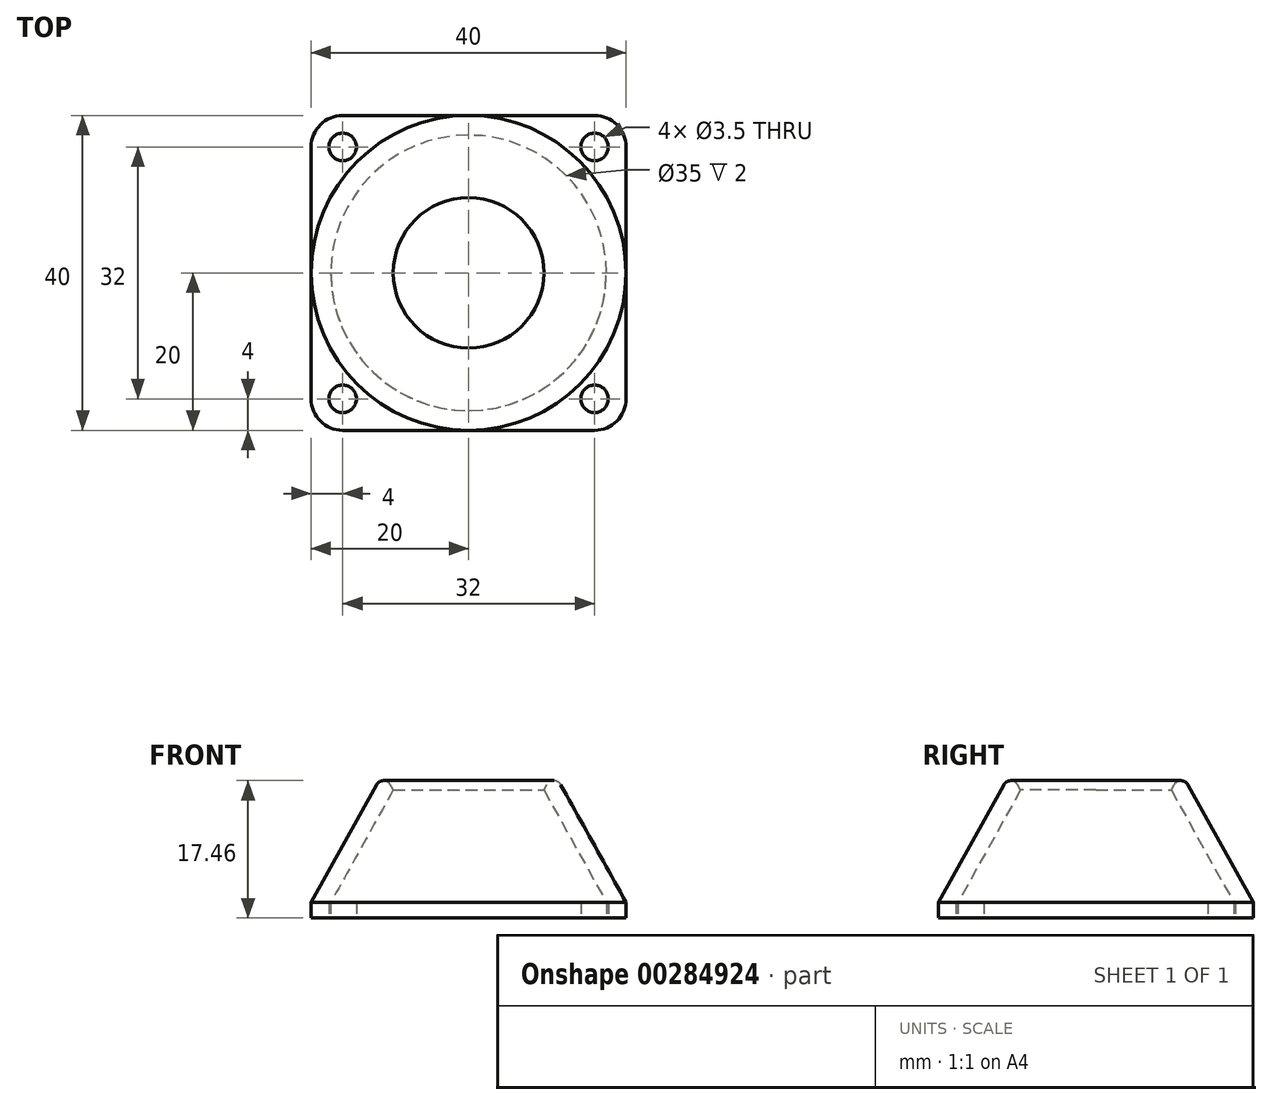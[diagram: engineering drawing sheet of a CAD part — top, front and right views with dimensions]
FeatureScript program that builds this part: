
annotation { "Feature Type Name" : "Feature", "Feature Type Description" : "" }
export const myFeature = defineFeature(function(context is Context, id is Id, definition is map)
    precondition{}
    {
        {
            var Q0;
            Q0=qCreatedBy(makeId("Top.planeOp"),FACE);
            var sketch = newSketch(context, id + "F0", { "sketchPlane" : qUnion([Q0])});
            skCircle(sketch, "E0", {"center": v(0, 0) * mm, "radius": 17.5 * mm});
            skLineSegment(sketch, "E1.bottom", {"start": v(20, 20) * mm, "end": v(-20, 20) * mm});
            skLineSegment(sketch, "E1.top", {"start": v(20, -20) * mm, "end": v(-20, -20) * mm});
            skLineSegment(sketch, "E1.left", {"start": v(20, 20) * mm, "end": v(20, -20) * mm});
            skLineSegment(sketch, "E1.right", {"start": v(-20, 20) * mm, "end": v(-20, -20) * mm});
            skSolve(sketch);
        }
        {
            var Q0;
            Q0 = qSketchRegion(id + "F0", true);
            extrude(context, id + "F1", {"entities" : qUnion([Q0]), "depth" : 2 * mm});
        }
        {
            var Q0;
            Q0=qCreatedBy(makeId("Front.planeOp"),FACE);
            var sketch = newSketch(context, id + "F2", { "sketchPlane" : qUnion([Q0])});
            skLineSegment(sketch, "E2.0.0", {"start": v(-20, 0) * mm, "end": v(20, 0) * mm, "construction": true});
            skLineSegment(sketch, "E2.0.1", {"start": v(20, 0) * mm, "end": v(20, 2) * mm, "construction": true});
            skLineSegment(sketch, "E2.0.2", {"start": v(20, 2) * mm, "end": v(-20, 2) * mm, "construction": true});
            skLineSegment(sketch, "E2.0.3", {"start": v(-20, 2) * mm, "end": v(-20, 0) * mm, "construction": true});
            skLineSegment(sketch, "E3", {"start": v(-17.5, 0) * mm, "end": v(-17.5, 2) * mm, "construction": true});
            skLineSegment(sketch, "E4", {"start": v(17.5, 2) * mm, "end": v(17.5, 0) * mm, "construction": true});
            skLineSegment(sketch, "E5", {"start": v(0, 0) * mm, "end": v(0, 20) * mm, "construction": true});
            skPoint(sketch, "E5.endSnap0", {"position": v(0, 2) * mm});
            skLineSegment(sketch, "E6", {"start": v(20, 2) * mm, "end": v(10, 20) * mm});
            skLineSegment(sketch, "E7", {"start": v(10, 20) * mm, "end": v(7.5, 20) * mm});
            skLineSegment(sketch, "E8", {"start": v(7.5, 20) * mm, "end": v(17.5, 2) * mm});
            skLineSegment(sketch, "E9", {"start": v(17.5, 2) * mm, "end": v(20, 2) * mm});
            skSolve(sketch);
        }
        {
            var Q0;
            Q0 = qSketchRegion(id + "F2", true);
            var Q1;
            Q1=sQuery(id+"F2.wireOp",EDGE,"E5");
            revolve(context, id + "F3", {"operationType" : NewBodyOperationType.ADD, "entities" : qUnion([Q0]), "axis" : qUnion([Q1]), "revolveType" : RevolveType.FULL});
        }
        {
            var Q0;
            Q0=makeQuery(id+"F3.opRevolve","SWEPT_EDGE",EDGE,{"disambiguationData":[OSD([sQuery(id+"F2.wireOp",EDGE,"E7"),sQuery(id+"F2.wireOp",EDGE,"E8")])]});
            chamfer(context, id + "F4", {"entities" : qUnion([Q0]), "width" : 2.5 * mm, "tangentPropagation" : true});
        }
        {
            var Q0;
            Q0=makeQuery(id+"F1.opExtrude","CAP_FACE",FACE,{"disambiguationData":[OSD([sQuery(id+"F0.wireOp",EDGE,"E0"),sQuery(id+"F0.wireOp",EDGE,"E1.bottom"),sQuery(id+"F0.wireOp",EDGE,"E1.top"),sQuery(id+"F0.wireOp",EDGE,"E1.left"),sQuery(id+"F0.wireOp",EDGE,"E1.right")])],"isStart":true});
            var sketch = newSketch(context, id + "F5", { "sketchPlane" : qUnion([Q0])});
            skCircle(sketch, "E10", {"center": v(-16, 16) * mm, "radius": 1.75 * mm});
            skLineSegment(sketch, "E11", {"start": v(0, 20) * mm, "end": v(0, -20) * mm, "construction": true});
            skLineSegment(sketch, "E12", {"start": v(20, 0) * mm, "end": v(-20, 0) * mm, "construction": true});
            skCircle(sketch, "E13.MirrorC", {"center": v(16, 16) * mm, "radius": 1.75 * mm});
            skCircle(sketch, "E14.MirrorC", {"center": v(16, -16) * mm, "radius": 1.75 * mm});
            skCircle(sketch, "E15.MirrorC", {"center": v(-16, -16) * mm, "radius": 1.75 * mm});
            skSolve(sketch);
        }
        {
            var Q0;
            Q0 = qSketchRegion(id + "F5", true);
            extrude(context, id + "F6", {"entities" : qUnion([Q0]), "operationType" : NewBodyOperationType.REMOVE, "endBound" : BoundingType.THROUGH_ALL, "oppositeDirection" : true, "depth" : 25 * mm});
        }
        {
            var Q0;
            Q0=makeQuery(id+"F1.opExtrude","SWEPT_EDGE",EDGE,{"disambiguationData":[OSD([sQuery(id+"F0.wireOp",EDGE,"E1.bottom"),sQuery(id+"F0.wireOp",EDGE,"E1.right")])]});
            var Q1;
            Q1=makeQuery(id+"F1.opExtrude","SWEPT_EDGE",EDGE,{"disambiguationData":[OSD([sQuery(id+"F0.wireOp",EDGE,"E1.top"),sQuery(id+"F0.wireOp",EDGE,"E1.right")])]});
            var Q2;
            Q2=makeQuery(id+"F1.opExtrude","SWEPT_EDGE",EDGE,{"disambiguationData":[OSD([sQuery(id+"F0.wireOp",EDGE,"E1.bottom"),sQuery(id+"F0.wireOp",EDGE,"E1.left")])]});
            var Q3;
            Q3=makeQuery(id+"F1.opExtrude","SWEPT_EDGE",EDGE,{"disambiguationData":[OSD([sQuery(id+"F0.wireOp",EDGE,"E1.top"),sQuery(id+"F0.wireOp",EDGE,"E1.left")])]});
            fillet(context, id + "F7", {"entities" : qUnion([Q0, Q1, Q2, Q3]), "radius" : 4 * mm, "tangentPropagation" : true, "allowEdgeOverflow" : false});
        }
        {
            var Q0;
            Q0=makeQuery(id+"F4.opChamfer","BLEND_EDGE",EDGE,{"blendedFrom":[makeQuery(id+"F3.opRevolve","SWEPT_EDGE",EDGE,{"disambiguationData":[OSD([sQuery(id+"F2.wireOp",EDGE,"E7"),sQuery(id+"F2.wireOp",EDGE,"E8")])]}),makeQuery(id+"F3.opRevolve","SWEPT_FACE",FACE,{"disambiguationData":[OSD([sQuery(id+"F2.wireOp",EDGE,"E6")])]})],"blendedInto":[makeQuery(id+"F3.opRevolve","SWEPT_FACE",FACE,{"disambiguationData":[OSD([sQuery(id+"F2.wireOp",EDGE,"E6")])]})]});
            fillet(context, id + "F8", {"entities" : qUnion([Q0]), "radius" : 1 * mm, "tangentPropagation" : true, "allowEdgeOverflow" : false});
        }
    });
